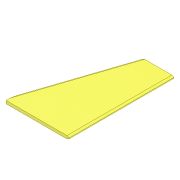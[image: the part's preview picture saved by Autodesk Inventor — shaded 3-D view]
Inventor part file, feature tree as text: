
AUTODESK INVENTOR PART (.ipt)
format: ipt  version: 2022 (Build 260153000, 153)  size: 121,344 bytes
history: native  units: mm
features: chamfer x4, extrude x3, sketch x3, plane x1, projected_geometry x1
ambient origin geometry x8: Origin, YZ Plane, XZ Plane, XY Plane, X Axis, Y Axis, Z Axis, Center Point
bodies: Solid1 (feature_tree)
feature tree (12):
  extrude  "Extrusion1"  Depth=600.0mm
  extrude  "Extrusion2"  Depth=28.0mm TaperAngle=0.0deg
  plane  "Work Plane1"
  extrude  "Extrusion3"  Depth=100.0mm
  chamfer  "Chamfer1"  Distance=16.0mm
  chamfer  "Chamfer2"  Distance=305.0mm
  chamfer  "Chamfer3"  Distance=20.0mm
  chamfer  "Chamfer4"  Distance=16.0mm
  sketch  "Sketch1"  dims[d0=1000.0mm d1=600.0mm]
  sketch  "Sketch2"  dims[d2=28.0mm d3=0.0mm d5=200.0mm d6=0.0mm]
  projected_geometry  "Projected Loop1"
  sketch  "Sketch3"  dims[d7=300.0mm d8=100.0mm d9=16.0mm d10=305.0mm d11=20.0mm d12=16.0mm d13=395.0mm d14=20.0mm d15=16.0mm d16=350.0mm d17=75.0mm d18=16.0mm d19=350.0mm d20=160.0mm d21=200.0mm d22=0.0mm d23=20.0mm d24=10.0mm d25=45.0deg d26=10.0mm d27=20.0mm d28=45.0deg d29=20.0mm d30=10.0mm d31=45.0deg d32=20.0mm d33=10.0mm d34=45.0deg]
